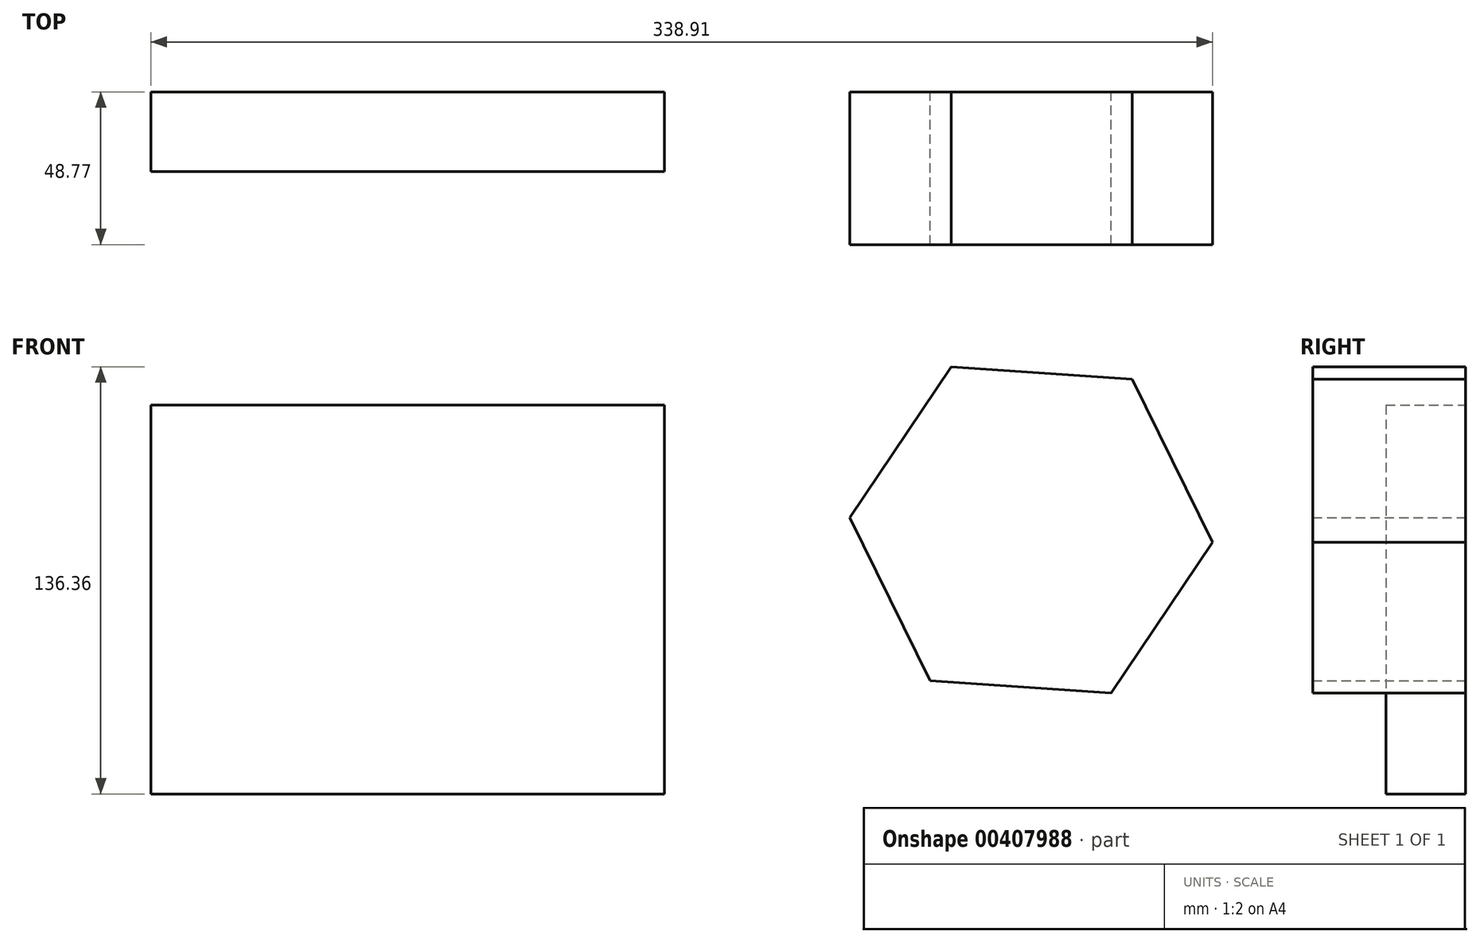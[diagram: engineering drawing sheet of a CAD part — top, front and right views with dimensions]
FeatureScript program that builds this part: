
annotation { "Feature Type Name" : "Feature", "Feature Type Description" : "" }
export const myFeature = defineFeature(function(context is Context, id is Id, definition is map)
    precondition{}
    {
        {
            var Q0;
            Q0=qCreatedBy(makeId("Front.planeOp"),FACE);
            var sketch = newSketch(context, id + "F0", { "sketchPlane" : qUnion([Q0])});
            skLineSegment(sketch, "E0.bottom", {"start": v(-75.74, 53.16) * mm, "end": v(88.25, 53.16) * mm});
            skLineSegment(sketch, "E0.top", {"start": v(-75.74, -70.94) * mm, "end": v(88.25, -70.94) * mm});
            skLineSegment(sketch, "E0.left", {"start": v(-75.74, 53.16) * mm, "end": v(-75.74, -70.94) * mm});
            skLineSegment(sketch, "E0.right", {"start": v(88.25, 53.16) * mm, "end": v(88.25, -70.94) * mm});
            skSolve(sketch);
        }
        {
            var Q0;
            Q0=makeQuery(id+"F0.imprint","IMPRINT",FACE,{"disambiguationData":[TD([[makeQuery(id+"F0.imprint","IMPRINT",EDGE,{"derivedFrom":sQuery(id+"F0.wireOp",EDGE,"E0.bottom")}),-1.0]])]});
            extrude(context, id + "F1", {"entities" : qUnion([Q0]), "depth" : 25.4 * mm});
        }
        {
            var Q0;
            Q0=qCreatedBy(makeId("Front.planeOp"),FACE);
            var sketch = newSketch(context, id + "F2", { "sketchPlane" : qUnion([Q0])});
            skCircle(sketch, "E1.cCircle", {"center": v(205.29, 13.35) * mm, "radius": 50.24 * mm, "construction": true});
            skLineSegment(sketch, "E1.0", {"start": v(263.17, 9.46) * mm, "end": v(230.86, -38.72) * mm});
            skLineSegment(sketch, "E1.1", {"start": v(230.86, -38.72) * mm, "end": v(172.98, -34.83) * mm});
            skLineSegment(sketch, "E1.2", {"start": v(172.98, -34.83) * mm, "end": v(147.41, 17.24) * mm});
            skLineSegment(sketch, "E1.3", {"start": v(147.41, 17.24) * mm, "end": v(179.72, 65.42) * mm});
            skLineSegment(sketch, "E1.4", {"start": v(179.72, 65.42) * mm, "end": v(237.6, 61.53) * mm});
            skLineSegment(sketch, "E1.5", {"start": v(237.6, 61.53) * mm, "end": v(263.17, 9.46) * mm});
            skPoint(sketch, "E1.0.midPoint", {"position": v(247.01, -14.63) * mm});
            skSolve(sketch);
        }
        {
            var Q0;
            Q0 = qSketchRegion(id + "F2", true);
            extrude(context, id + "F3", {"entities" : qUnion([Q0]), "operationType" : NewBodyOperationType.ADD, "depth" : 48.77 * mm});
        }
    });
